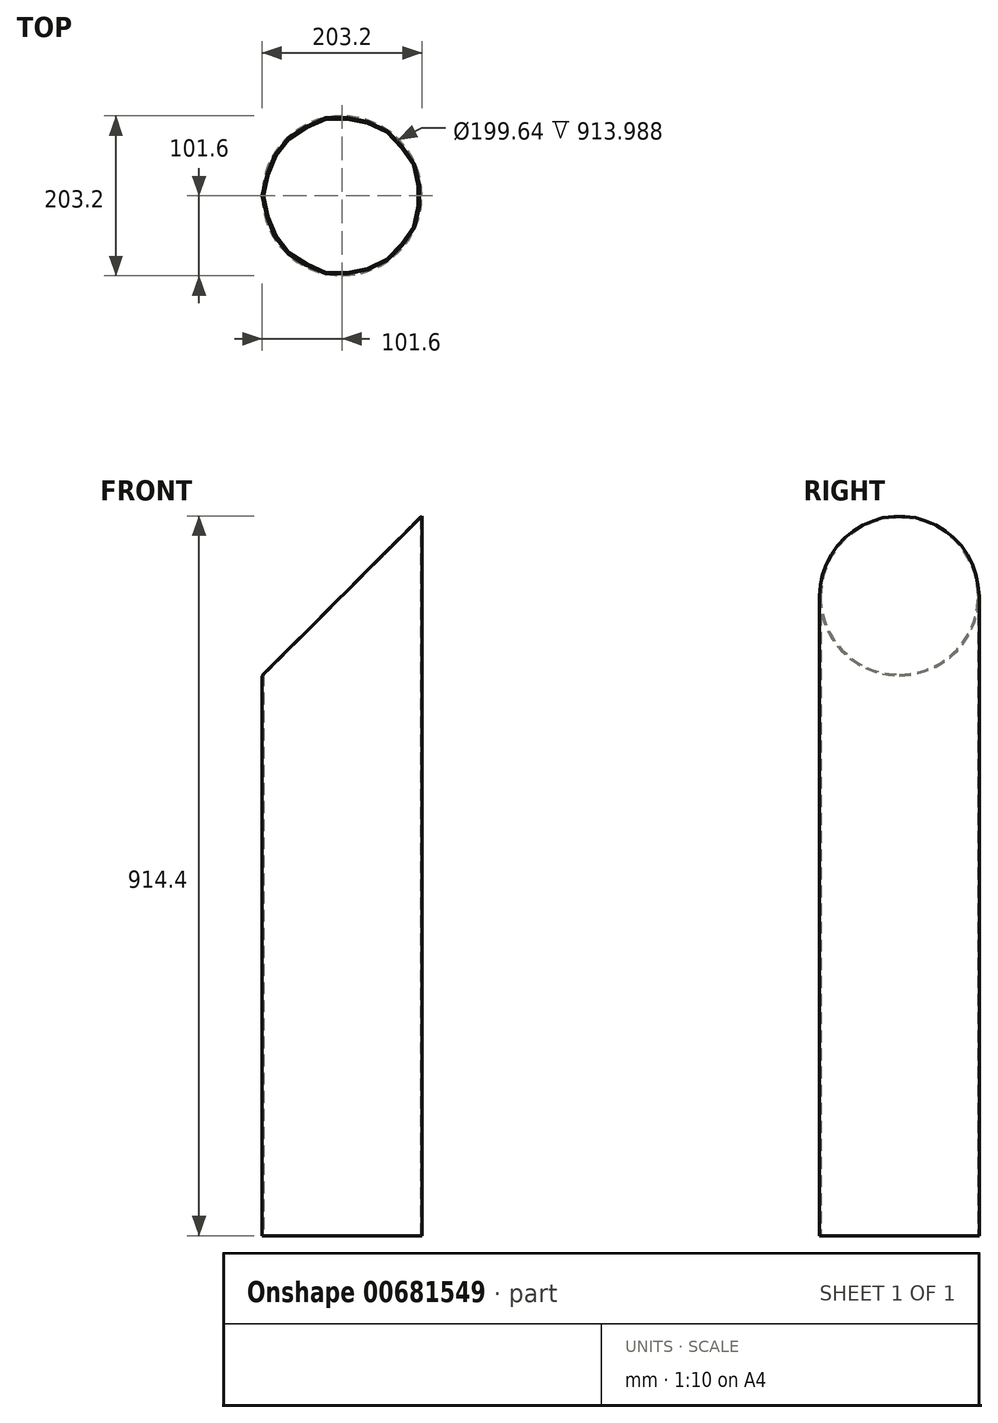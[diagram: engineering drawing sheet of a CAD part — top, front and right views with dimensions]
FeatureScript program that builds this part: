
annotation { "Feature Type Name" : "Feature", "Feature Type Description" : "" }
export const myFeature = defineFeature(function(context is Context, id is Id, definition is map)
    precondition{}
    {
        {
            var Q0;
            Q0=qCreatedBy(makeId("Top.planeOp"),FACE);
            var sketch = newSketch(context, id + "F0", { "sketchPlane" : qUnion([Q0])});
            skCircle(sketch, "E0", {"center": v(0, 0) * mm, "radius": 101.6 * mm});
            skCircle(sketch, "E1.0", {"center": v(0, 0) * mm, "radius": 99.82 * mm});
            skSolve(sketch);
        }
        {
            var Q0;
            Q0 = qSketchRegion(id + "F0", true);
            extrude(context, id + "F1", {"entities" : qUnion([Q0]), "depth" : 914.4 * mm, "offsetDistance" : 25.4 * mm});
        }
        {
            var Q0;
            Q0=qCreatedBy(makeId("Front.planeOp"),FACE);
            var sketch = newSketch(context, id + "F2", { "sketchPlane" : qUnion([Q0])});
            skLineSegment(sketch, "E2.top", {"start": v(101.6, 711.2) * mm, "end": v(-101.6, 711.2) * mm});
            skLineSegment(sketch, "E2.right", {"start": v(-101.6, 914.4) * mm, "end": v(-101.6, 711.2) * mm});
            skLineSegment(sketch, "E3", {"start": v(-101.6, 711.2) * mm, "end": v(101.6, 914.4) * mm});
            skLineSegment(sketch, "E4", {"start": v(-101.6, 914.4) * mm, "end": v(101.6, 914.4) * mm});
            skSolve(sketch);
        }
        {
            var Q0;
            Q0 = qSketchRegion(id + "F2", true);
            extrude(context, id + "F3", {"entities" : qUnion([Q0]), "operationType" : NewBodyOperationType.REMOVE, "endBound" : BoundingType.THROUGH_ALL, "oppositeDirection" : true, "depth" : 25.4 * mm, "offsetDistance" : 25.4 * mm, "hasSecondDirection" : true, "secondDirectionBound" : SecondDirectionBoundingType.THROUGH_ALL, "secondDirectionOppositeDirection" : false, "secondDirectionDepth" : 25.4 * mm});
        }
    });
